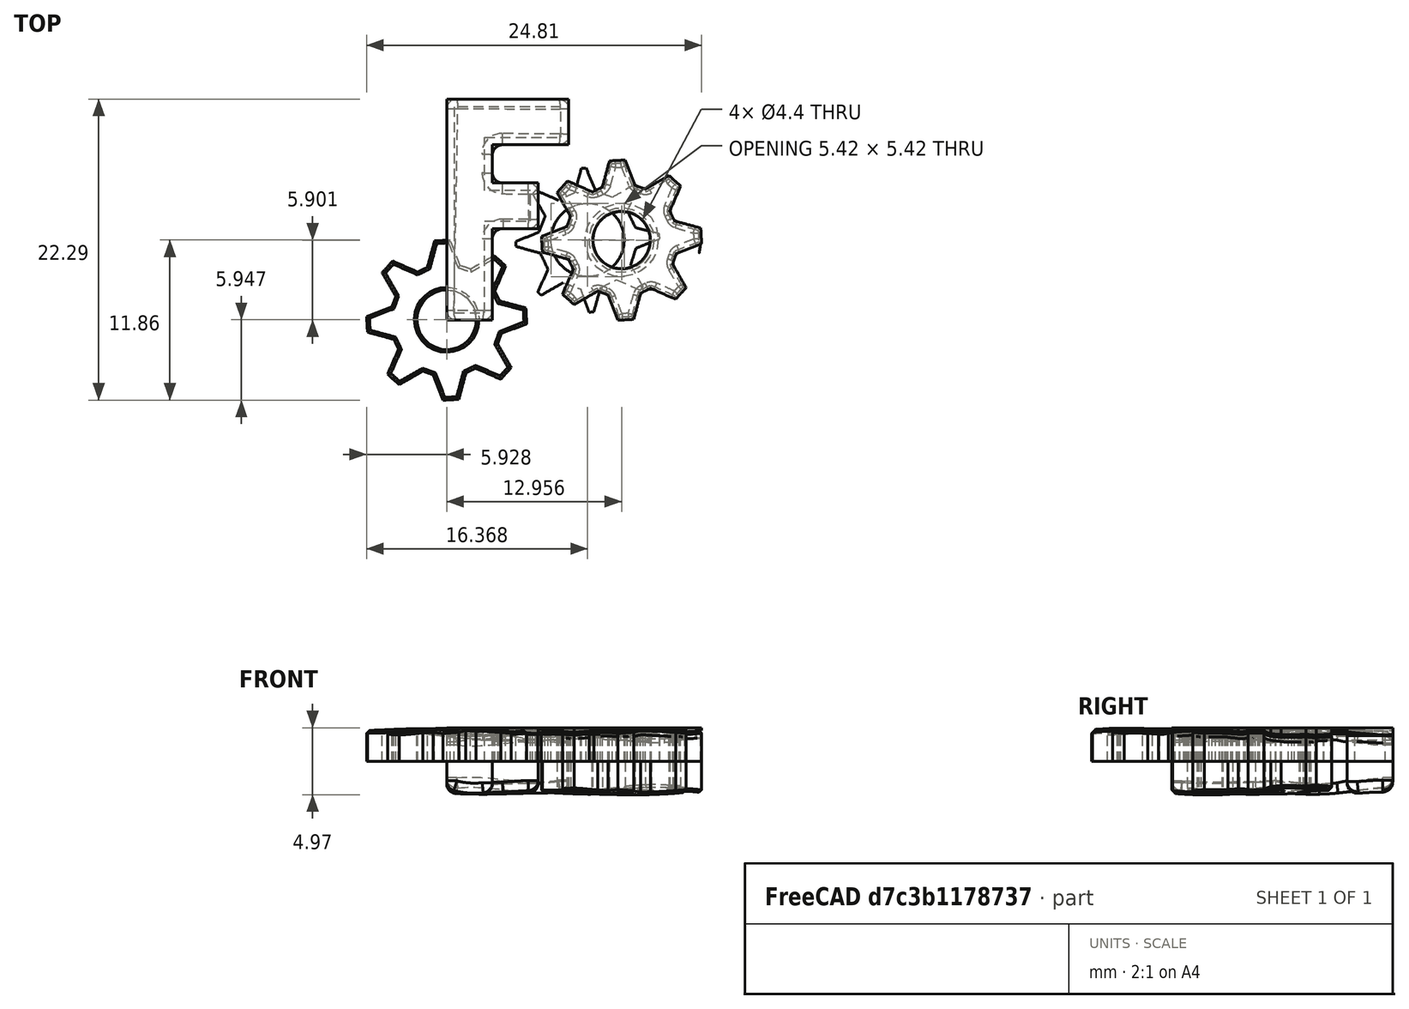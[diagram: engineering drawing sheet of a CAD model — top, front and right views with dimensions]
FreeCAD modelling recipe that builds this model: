
FCSTD DOCUMENT  (FreeCAD 0.19R24212 (Git))
Label: logo 3d
License: Creative Commons Attribution
LicenseURL: http://creativecommons.org/licenses/by/4.0/
objects: Part::FeaturePython×14, Part::Feature×10, App::DocumentObjectGroup×6, Part::Extrusion×5, Part::Part2DObjectPython×4, Part::Cut×3, Part::Fillet×2, Part::Chamfer×2, Part::Mirroring×2, Part::RuledSurface×1, Part::Loft×1, Part::Sweep×1, Part::Cylinder×1
note: 46 computed .brp shape members not serialized (recipe doc carries the construction recipe); baked Part::Feature solids carry a one-line shape summary decoded from their .brp

FEATURE [Part::Feature] Face
  shape: bbox 7.902 x 15.24 x 2e-07 mm, 1 faces, 0 solids (baked)
FEATURE [Part::Extrusion] Extrusion
  Base = -> Face
  Dir = (0,0,2)
  DirMode = 0
  FaceMakerClass = Part::FaceMakerBullseye
  LengthFwd = 0
  LengthRev = 0
  Solid = true
  Symmetric = false
FEATURE [Part::Feature] Face001
  shape: bbox 10.67 x 10.67 x 2e-07 mm, 1 faces, 0 solids (baked)
FEATURE [Part::Feature] Face002
  shape: bbox 5.417 x 5.417 x 2.595e-07 mm, 1 faces, 0 solids (baked)
FEATURE [Part::Cut] Cut
  Base = -> Face001
  Refine = true
  Tool = -> Face002
FEATURE [Part::Extrusion] Extrusion001
  Base = -> Cut
  Dir = (0,0,2)
  DirMode = 0
  FaceMakerClass = Part::FaceMakerBullseye
  LengthFwd = 0
  LengthRev = 0
  Solid = true
  Symmetric = false
FEATURE [Part::Feature] Face003
  shape: bbox 9.031 x 16.37 x 2e-07 mm, 1 faces, 0 solids (baked)
FEATURE [Part::Feature] Face004
  shape: bbox 11.85 x 11.85 x 2e-07 mm, 1 faces, 0 solids (baked)
FEATURE [Part::Feature] Face005
  shape: bbox 4.236 x 4.236 x 2e-07 mm, 1 faces, 0 solids (baked)
FEATURE [Part::Cut] Cut001
  Base = -> Face004
  Refine = true
  Tool = -> Face005
FEATURE [Part::Extrusion] Extrusion002  label="F"
  Base = -> Face003
  Dir = (0,0,2.5)
  DirMode = 0
  FaceMakerClass = Part::FaceMakerBullseye
  LengthFwd = 0
  LengthRev = 0
  Solid = true
  Symmetric = false
FEATURE [Part::Extrusion] Extrusion003  label="Gear"
  Base = -> Cut001
  Dir = (0,0,2.5)
  DirMode = 0
  FaceMakerClass = Part::FaceMakerBullseye
  LengthFwd = 0
  LengthRev = 0
  Placement = pos=(2.50715,0,0) rot=(0,0,1;0rad)
  Solid = true
  Symmetric = false
FEATURE [Part::Part2DObjectPython] BSpline  # Draft 2D object (typed FeaturePython)
  Area = 0
  Closed = false
  MakeFace = true
  Parameterization = 1
  Points = (4) [(-0.921562,-1.30653e-07,1.28599),(2.81511,3.99108e-07,2.2513),(6.20925,8.80307e-07,1.64409),(9.69333,1.37426e-06,2.25)]
FEATURE [Part::Extrusion] Extrude
  Base = -> BSpline
  Dir = (0,1,0)
  DirMode = 0
  FaceMakerClass = Part::FaceMakerBullseye
  LengthFwd = 20
  LengthRev = 0
  Solid = false
  Symmetric = false
FEATURE [Part::FeaturePython] Slice  # WARN: FeaturePython — macro-defined, semantics opaque (R4)
  Base = -> Extrusion002
  Mode = 1
  Tolerance = 0
  Tools = -> [Extrude]
FEATURE [Part::FeaturePython] Slice_child0  label="Slice.0"  # WARN: FeaturePython — macro-defined, semantics opaque (R4)
  Base = -> Slice
  FilterType = 1
  Invert = false
  OverrideMaxVal = 0
  WindowFrom = 80
  WindowTo = 100
  items = 0
FEATURE [Part::FeaturePython] Slice_child1  label="Slice.1"  # WARN: FeaturePython — macro-defined, semantics opaque (R4)
  Base = -> Slice
  FilterType = 1
  Invert = false
  OverrideMaxVal = 0
  WindowFrom = 80
  WindowTo = 100
  items = 1
FEATURE [App::DocumentObjectGroup] GrExplode_Slice  label="Exploded Slice"
  Group = -> [Slice_child0,Slice_child1]
FEATURE [Part::Part2DObjectPython] BSpline001  # Draft 2D object (typed FeaturePython)
  Area = 0
  Closed = false
  MakeFace = true
  Parameterization = 1
  Points = (4) [(9.8506,16.3689,1.62953),(6.40885,16.3689,2.27964),(2.78864,16.3689,1.92271),(-0.806085,16.3689,2.34337)]
FEATURE [Part::RuledSurface] Ruled_Surface
  Curve1 = -> BSpline [Edge1]
  Curve2 = -> BSpline001 [Edge1]
  Orientation = 0
FEATURE [Part::Loft] Loft
  Closed = false
  MaxDegree = 5
  Ruled = false
  Sections = -> [BSpline,BSpline001]
  Solid = false
FEATURE [Part::FeaturePython] Slice001  # WARN: FeaturePython — macro-defined, semantics opaque (R4)
  Base = -> Extrusion002
  Mode = 1
  Tolerance = 0
  Tools = -> [Ruled_Surface]
FEATURE [Part::FeaturePython] Slice001_child0  label="Slice001.0"  # WARN: FeaturePython — macro-defined, semantics opaque (R4)
  Base = -> Slice001
  FilterType = 1
  Invert = false
  OverrideMaxVal = 0
  WindowFrom = 80
  WindowTo = 100
  items = 0
FEATURE [Part::FeaturePython] Slice001_child1  label="Slice001.1"  # WARN: FeaturePython — macro-defined, semantics opaque (R4)
  Base = -> Slice001
  FilterType = 1
  Invert = false
  OverrideMaxVal = 0
  WindowFrom = 80
  WindowTo = 100
  items = 1
FEATURE [App::DocumentObjectGroup] GrExplode_Slice001  label="Exploded Slice001"
  Group = -> [Slice001_child0,Slice001_child1]
FEATURE [Part::Part2DObjectPython] BSpline002  # Draft 2D object (typed FeaturePython)
  Area = 0
  Closed = false
  MakeFace = true
  Parameterization = 1
  Points = (6) [(5,-0.221376,1.48038),(5,3.53438,1.79946),(5,6.88044,1.87913),(5,11.6481,2.19663),(5,15.5631,1.94131),(5,18.4568,2.25337)]
FEATURE [Part::Sweep] Sweep
  Frenet = false
  Sections = -> [BSpline,BSpline001]
  Solid = false
  Spine = -> BSpline002 [Edge1]
  Transition = 1
FEATURE [Part::FeaturePython] Slice002  # WARN: FeaturePython — macro-defined, semantics opaque (R4)
  Base = -> Extrusion002
  Mode = 1
  Tolerance = 0
  Tools = -> [Sweep]
FEATURE [Part::FeaturePython] Slice002_child0  label="Slice002.0"  # WARN: FeaturePython — macro-defined, semantics opaque (R4)
  Base = -> Slice002
  FilterType = 1
  Invert = false
  OverrideMaxVal = 0
  WindowFrom = 80
  WindowTo = 100
  items = 0
FEATURE [Part::FeaturePython] Slice002_child1  label="Slice002.1"  # WARN: FeaturePython — macro-defined, semantics opaque (R4)
  Base = -> Slice002
  FilterType = 1
  Invert = false
  OverrideMaxVal = 0
  WindowFrom = 80
  WindowTo = 100
  items = 1
FEATURE [App::DocumentObjectGroup] GrExplode_Slice002  label="Exploded Slice002"
  Group = -> [Slice002_child0,Slice002_child1]
FEATURE [Part::Fillet] Fillet
  Base = -> Slice002_child0
  Edges = 20 edges r=0.75: [Edge2,Edge3,Edge4,Edge14,Edge15,Edge16,Edge17,Edge18,Edge19,Edge20,Edge21,Edge22,Edge23,Edge24,Edge25,Edge26,Edge27,Edge28,Edge29,Edge30]
FEATURE [Part::FeaturePython] Clone  label="Sweep001"  # Draft clone (typed FeaturePython)
  AttacherType = Attacher::AttachEngine3D
  Fuse = false
  Objects = -> [Sweep]
  Placement = pos=(-0.267949,4.4641,0) rot=(0,0,1;5.23599rad)
  Scale = (1.5,1,1)
FEATURE [Part::FeaturePython] Slice003  # WARN: FeaturePython — macro-defined, semantics opaque (R4)
  Base = -> Extrusion003
  Mode = 1
  Tolerance = 0
  Tools = -> [Clone]
FEATURE [Part::FeaturePython] Slice003_child0  label="Slice003.0"  # WARN: FeaturePython — macro-defined, semantics opaque (R4)
  Base = -> Slice003
  FilterType = 1
  Invert = false
  OverrideMaxVal = 0
  WindowFrom = 80
  WindowTo = 100
  items = 0
FEATURE [Part::FeaturePython] Slice003_child1  label="Slice003.1"  # WARN: FeaturePython — macro-defined, semantics opaque (R4)
  Base = -> Slice003
  FilterType = 1
  Invert = false
  OverrideMaxVal = 0
  WindowFrom = 80
  WindowTo = 100
  items = 1
FEATURE [Part::Cylinder] Cylinder  label="Cylindre"
  Angle = 360
  AttacherType = Attacher::AttachEngine3D
  Height = 10
  Placement = pos=(12.9536,5.92863,0) rot=(0,0,1;0rad)
  Radius = 2.2
FEATURE [Part::Cut] Cut002
  Base = -> Slice003_child0
  Refine = true
  Tool = -> Cylinder
FEATURE [App::DocumentObjectGroup] GrExplode_Slice003  label="Exploded Slice003"
  Group = -> [Slice003_child1,Cut002]
FEATURE [Part::Fillet] Fillet001
  Base = -> Cut002
  Edges = 66 edges r=0.5: [Edge2,Edge3,Edge4,Edge37,Edge38,Edge39,Edge40,Edge41,Edge42,Edge43,Edge44,Edge45,Edge46,Edge47,Edge48,Edge49,Edge50,Edge51,Edge52,Edge53,Edge54,Edge55,Edge56,Edge57,Edge58,Edge59,Edge60,Edge61,Edge62,Edge63,Edge64,Edge65,Edge66,Edge67,Edge68,Edge69,Edge70,Edge71,Edge72,Edge73,Edge74,Edge75,Edge76,+23 more]
FEATURE [Part::Chamfer] Chamfer
  Base = -> Cut002
  Edges = 65 edges r=0.05: [Edge2,Edge3,Edge4,Edge37,Edge38,Edge39,Edge40,Edge41,Edge42,Edge43,Edge44,Edge45,Edge46,Edge47,Edge48,Edge49,Edge50,Edge51,Edge52,Edge53,Edge55,Edge56,Edge57,Edge58,Edge59,Edge60,Edge61,Edge62,Edge63,Edge64,Edge65,Edge66,Edge67,Edge68,Edge69,Edge70,Edge71,Edge72,Edge73,Edge74,Edge75,Edge76,Edge77,+22 more]
FEATURE [Part::Chamfer] Chamfer001
  Base = -> Cut002
  Edges = 34 edges r=0.2: [Edge3,Edge38,Edge39,Edge40,Edge41,Edge42,Edge43,Edge44,Edge45,Edge46,Edge47,Edge48,Edge49,Edge50,Edge51,Edge52,Edge53,Edge54,Edge55,Edge56,Edge57,Edge58,Edge59,Edge60,Edge61,Edge62,Edge63,Edge64,Edge65,Edge66,Edge67,Edge68,Edge69,Edge70]
FEATURE [App::DocumentObjectGroup] Groupe  label="Final"
  Group = -> [Fillet,Chamfer001]
FEATURE [Part::Mirroring] Part__Mirroring  label="Fillet (Mirror #1)"
  Base = (0,0,0)
  Normal = (0,0,1)
  Source = -> Fillet
FEATURE [Part::Mirroring] Part__Mirroring001  label="Chamfer001 (Mirror #2)"
  Base = (0,0,0)
  Normal = (0,0,1)
  Source = -> Chamfer001
FEATURE [App::DocumentObjectGroup] Groupe001  label="Mirror"
  Group = -> [Part__Mirroring,Part__Mirroring001]
FEATURE [Part::Feature] Chamfer001001
  Placement = pos=(-12.9522,-5.92264,0) rot=(0,0,1;0rad)
  shape: bbox 20.43 x 20.68 x 2.715 mm, 68 faces (baked)
FEATURE [Part::Feature] Chamfer001001001
  Placement = pos=(-12.9522,-5.92264,0) rot=(0,0,1;0rad)
  shape: bbox 20.43 x 20.68 x 2.715 mm, 68 faces (baked)
FEATURE [Part::FeaturePython] Clone001  label="Chamfer001001002"  # Draft clone (typed FeaturePython)
  AttacherType = Attacher::AttachEngine3D
  Fuse = false
  Objects = -> [Chamfer001001]
  Placement = pos=(-12.9522,-5.92264,0) rot=(0,0,1;0rad)
  Scale = (1,1,1)
FEATURE [Part::Feature] Fillet002
  shape: bbox 10.79 x 18.77 x 2.834 mm, 42 faces (baked)
FEATURE [Part::Part2DObjectPython] Line  # Draft 2D object (typed FeaturePython)
  Area = 0
  ChamferSize = 0
  Closed = false
  End = (13.2726,3.83127,0)
  FilletRadius = 0
  Length = 4.24294
  MakeFace = true
  Placement = pos=(12.6346,8.02598,0) rot=(0,0,1;0rad)
  Points = (2) [(0,0,0),(0.637937,-4.19471,0)]
  Start = (12.6346,8.02598,0)
  Subdivisions = 0
FEATURE [Part::Feature] Chamfer001001002  label="Chamfer001001003"
  shape: bbox 20.43 x 20.68 x 2.715 mm, 68 faces (baked)
